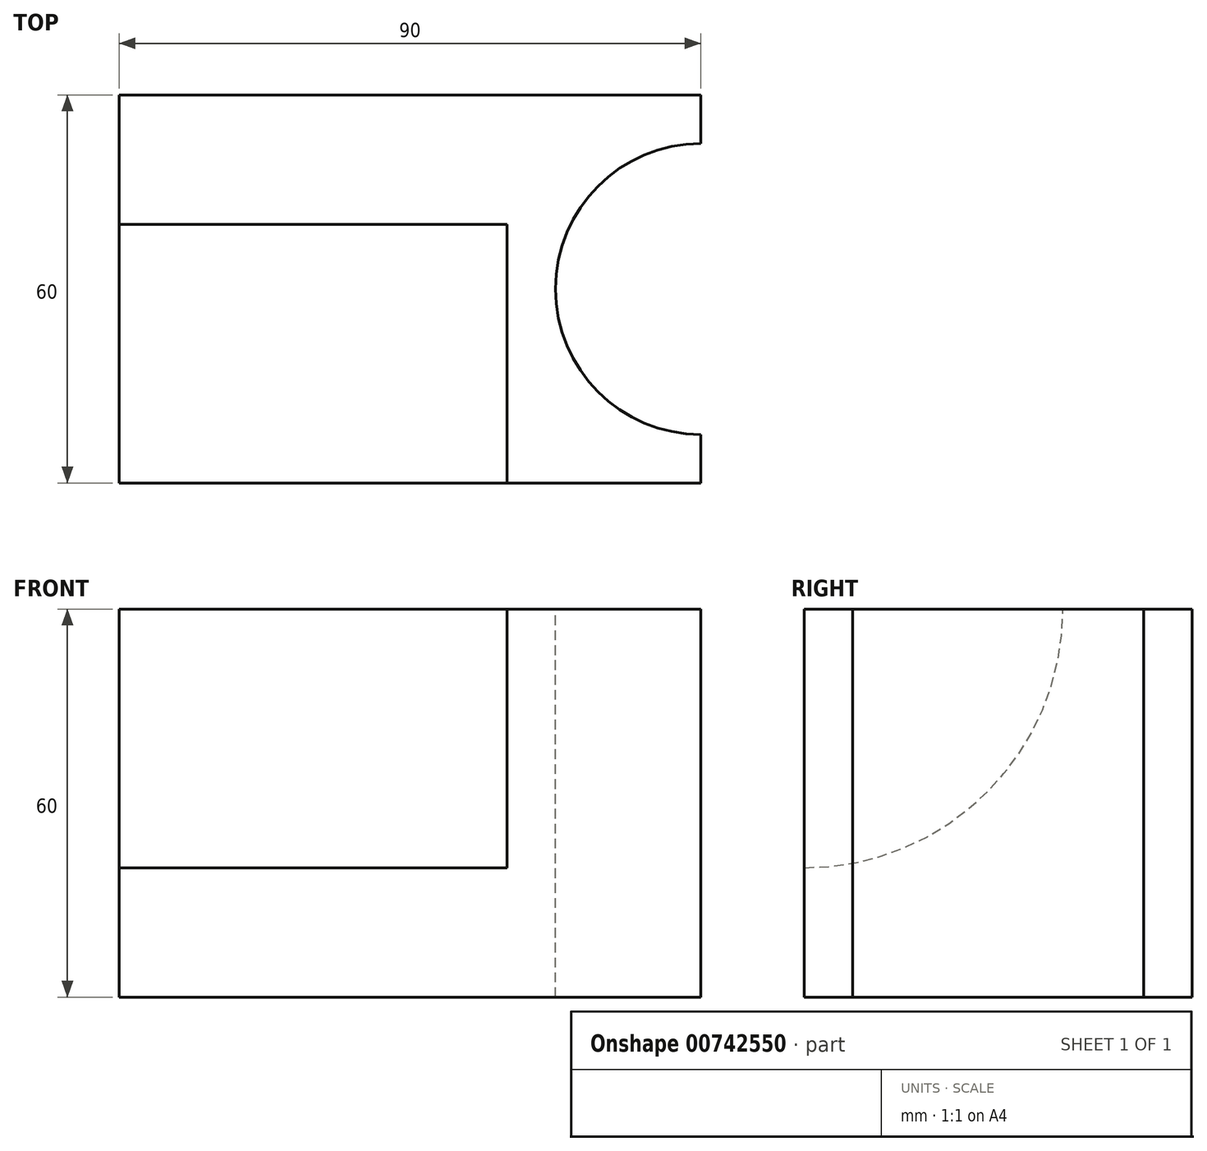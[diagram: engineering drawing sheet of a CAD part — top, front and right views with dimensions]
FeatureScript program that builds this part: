
annotation { "Feature Type Name" : "Feature", "Feature Type Description" : "" }
export const myFeature = defineFeature(function(context is Context, id is Id, definition is map)
    precondition{}
    {
        {
            var Q0;
            Q0=qCreatedBy(makeId("Front.planeOp"),FACE);
            var sketch = newSketch(context, id + "F0", { "sketchPlane" : qUnion([Q0])});
            skLineSegment(sketch, "E0.bottom", {"start": v(-90, 60) * mm, "end": v(0, 60) * mm});
            skLineSegment(sketch, "E0.top", {"start": v(-90, 0) * mm, "end": v(0, 0) * mm});
            skLineSegment(sketch, "E0.left", {"start": v(-90, 60) * mm, "end": v(-90, 0) * mm});
            skLineSegment(sketch, "E0.right", {"start": v(0, 60) * mm, "end": v(0, 0) * mm});
            skSolve(sketch);
        }
        {
            var Q0;
            Q0 = qSketchRegion(id + "F0", true);
            extrude(context, id + "F1", {"entities" : qUnion([Q0]), "depth" : 60 * mm, "offsetDistance" : 25 * mm});
        }
        {
            var Q0;
            Q0=makeQuery(id+"F1.opExtrude","SWEPT_FACE",FACE,{"disambiguationData":[OSD([sQuery(id+"F0.wireOp",EDGE,"E0.bottom")])]});
            var sketch = newSketch(context, id + "F2", { "sketchPlane" : qUnion([Q0])});
            skLineSegment(sketch, "E1", {"start": v(0, -52.5) * mm, "end": v(0, -7.5) * mm});
            skArc(sketch, "E2", {"start": v(0, -7.5) * mm, "mid": v(-22.5, -30) * mm, "end": v(0, -52.5) * mm});
            skSolve(sketch);
        }
        {
            var Q0;
            Q0 = qSketchRegion(id + "F2", true);
            extrude(context, id + "F3", {"entities" : qUnion([Q0]), "operationType" : NewBodyOperationType.REMOVE, "oppositeDirection" : true, "depth" : 228 * mm, "offsetDistance" : 25 * mm});
        }
        {
            var Q0;
            Q0=makeQuery(id+"F1.opExtrude","SWEPT_FACE",FACE,{"disambiguationData":[OSD([sQuery(id+"F0.wireOp",EDGE,"E0.left")])]});
            var sketch = newSketch(context, id + "F4", { "sketchPlane" : qUnion([Q0])});
            skArc(sketch, "E3", {"start": v(20, 60) * mm, "mid": v(31.72, 31.72) * mm, "end": v(60, 20) * mm});
            skSolve(sketch);
        }
        {
            var Q0;
            Q0 = qSketchRegion(id + "F4", true);
            var Q1;
            {var subQ0=sQuery(id+"F4.wireOp",EDGE,"E3");Q1=makeQuery(id+"F4.imprint","IMPRINT",FACE,{"disambiguationData":[TD([[makeQuery(id+"F4.imprint","IMPRINT",EDGE,{"derivedFrom":subQ0}),1.0]])]});}
            extrude(context, id + "F5", {"entities" : qUnion([Q0, Q1]), "operationType" : NewBodyOperationType.REMOVE, "oppositeDirection" : true, "depth" : 60 * mm, "offsetDistance" : 25 * mm});
        }
    });
